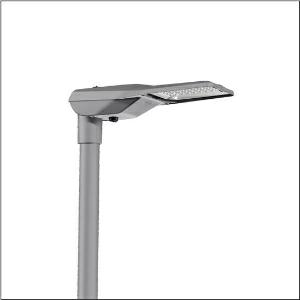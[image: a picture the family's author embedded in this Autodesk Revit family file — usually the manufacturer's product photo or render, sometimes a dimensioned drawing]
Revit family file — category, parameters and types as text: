
# Revit family: streetlight_sl_21_iq_mini___st0_8a_5xe2c31y08gb_e7ef
name_source: partatom
category: Lighting Fixtures
units: mm (PartAtom-declared; Revit-internal decimal feet)

## family parameters
Cut with Voids When Loaded = No
Host = Face
Light Source = No
Part Type = Normal
Room Calculation Point = No
Round Connector Dimension = Use Diameter
Shared = No

## types (1)
- --- (1 x LED, 5990 lm, 39.8 W, 3000K)
    Apparent Load = 40 VA
    CIE Flux Codes = 38 75 97 100 100
    Color Rendering = 70
    Color Temperature = 3000K
    Default Elevation = 1800 mm
    Description = Streetlight SL 21 iQ mini, mast luminaire, primary light control with lens, of PMMA, primary optical cover: cover, of toughened safety glass, transparent, light distribution: ST0.8a, light emission: direct distribution, primary light characteristic: asymmetric, installation type: post-top, side-entry, LED, High Power LED, rated luminous flux: 5.990lm, luminous efficacy: 151lm/W, light colour: 730, colour temperature: 3000K, control: presetting dimming logarithmic, Street-Remote, Auto-Match, Temp-Guard, Lumen-Switch, Night-Set, Smart-Wire, Light-Fading, Desk-Remote (wireless, voltage-free reading and setting of iQ features in the workshop via application-optimized NFC function/RFID function), optimised constant luminous flux control (CLO 2.0), mains connection: 220..240V, AC, 50/60Hz, start of lifetime: 40W, end of service life: 41W, reduction: 18W, luminaire housing, of diecast aluminium, powder-coated, Siteco® metallic grey (DB 702S), corrosivity category C5 mid according to DIN EN ISO 12944, please order mast flange separately, inclination adjustable: 0°, 5°, 10°, 15°, sealing non-destructively replaceable, multi-level sealing system, length: 628mm, width: 235mm, height: 110mm, mast flange for spigot size: 42mm (side-entry): 5XC10008XM4, 60/48mm (side-entry/post-top): 5XC10108XM2, 76/60mm (side-entry/post-top): 5XC10108XM1, Smart Interface below and above, protection rating (complete): IP66, insulation class (complete): insulation class II (safety insulation), certification: CE, ENEC, ENEC+, VDE, impact resistance: IK09, permissible operating ambient temperature for outdoor applications: -40..+50°C, standard-compliant lighting for roads and squares, packaging unit: 1 piece

Light Distribution: ST0.8a
    Height = 110 mm
    Lamp = 1 x LED
    Lamp Light Flux = 5990 lm
    Lamp Power = 39.8 W
    Lamp count = 1
    Length = 625 mm
    Luminous efficacy = 151 lm/W
    Manufacturer = Siteco
    ModVariant = No
    Model = 5XE2C31Y08GB
    Number of Poles = 1
    OnlyDefault = Yes
    Power Factor = 1
    Product Name = Streetlight SL 21 iQ mini | ST0.8a
    Product group = mast luminaire | pylon top
    ProductGroupID = 6100
    Protection Class = Protection class II
    Protection Degree = IP 66
    RLX_Detail_Level = 1
    RLX_Emergency_Light_Flux = 0 lm
    RLX_Emergency_Type = 0
    RLX_Emergency_Type_DB = No
    RlxData = <blob elided: 92929 chars, md5=04e5e0eb>
    Socket = socket
    Standby Power = 0 W
    System Light Flux = 5990 lm
    System Power = 40 W
    Type Comments = factory setting: luminous flux: 100 % | dim-lin: 254 | 800 mA
    Type Image = l_1003514.jpg
    URL = http://relux.com
    VarID = @adj_061543
    Voltage = 0 V
    Weight = 0.00 kg
    Width = 234 mm

## geometry (parser evidence)
native form markers: Blend x4, Sweep x12
no freeform markers — native parametric forms only
